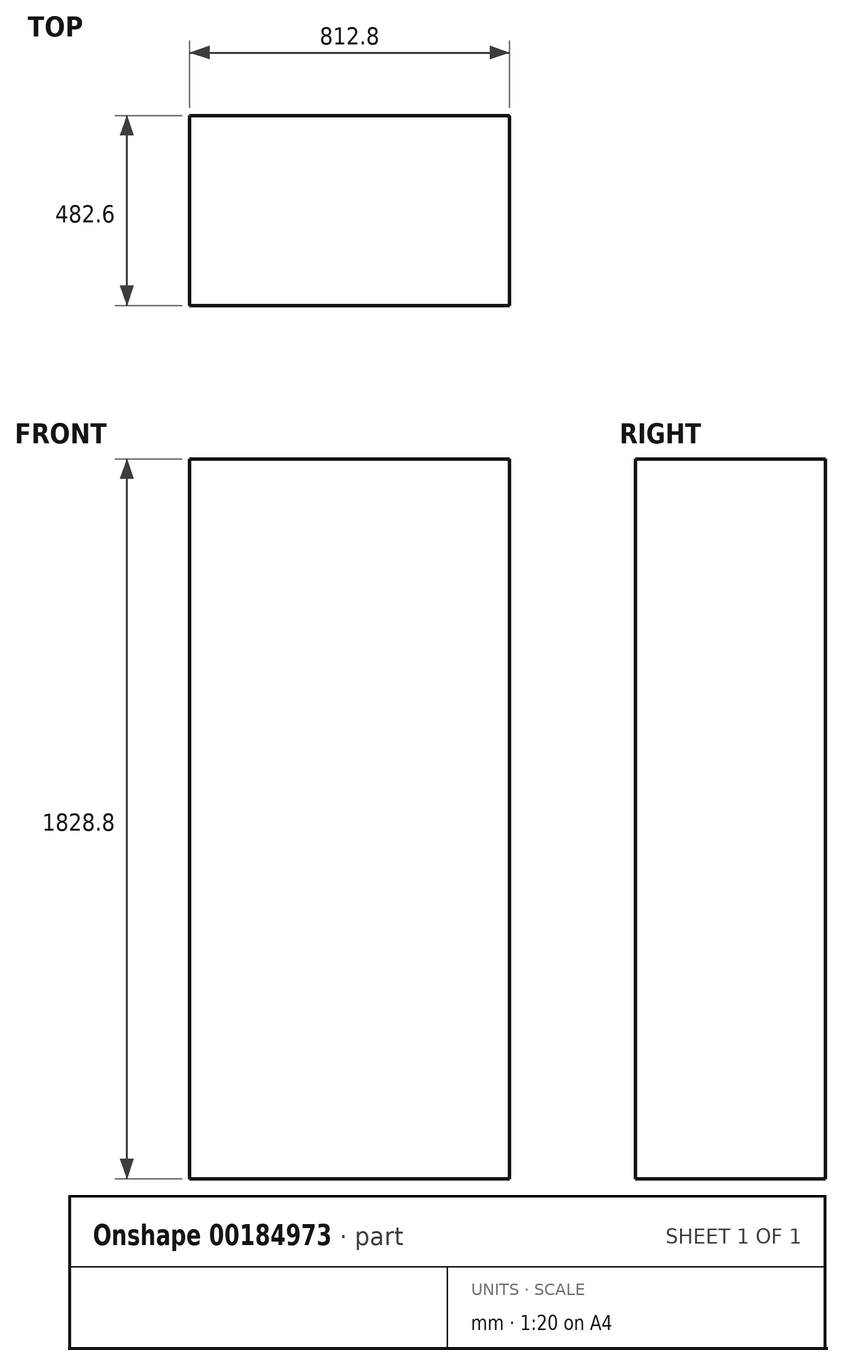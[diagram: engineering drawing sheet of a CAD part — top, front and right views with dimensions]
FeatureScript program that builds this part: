
annotation { "Feature Type Name" : "Feature", "Feature Type Description" : "" }
export const myFeature = defineFeature(function(context is Context, id is Id, definition is map)
    precondition{}
    {
        {
            var Q0;
            Q0=qCreatedBy(makeId("Top.planeOp"),FACE);
            var sketch = newSketch(context, id + "F0", { "sketchPlane" : qUnion([Q0])});
            skLineSegment(sketch, "E0.bottom", {"start": v(406.4, 241.3) * mm, "end": v(-406.4, 241.3) * mm});
            skLineSegment(sketch, "E0.top", {"start": v(406.4, -241.3) * mm, "end": v(-406.4, -241.3) * mm});
            skLineSegment(sketch, "E0.left", {"start": v(406.4, 241.3) * mm, "end": v(406.4, -241.3) * mm});
            skLineSegment(sketch, "E0.right", {"start": v(-406.4, 241.3) * mm, "end": v(-406.4, -241.3) * mm});
            skPoint(sketch, "E0.middle", {"position": v(0, 0) * mm});
            skSolve(sketch);
        }
        {
            var Q0;
            Q0=makeQuery(id+"F0.imprint","IMPRINT",FACE,{"disambiguationData":[TD([[makeQuery(id+"F0.imprint","IMPRINT",EDGE,{"derivedFrom":sQuery(id+"F0.wireOp",EDGE,"E0.bottom")}),1.0]])]});
            extrude(context, id + "F1", {"entities" : qUnion([Q0]), "depth" : 1828.8 * mm});
        }
    });
